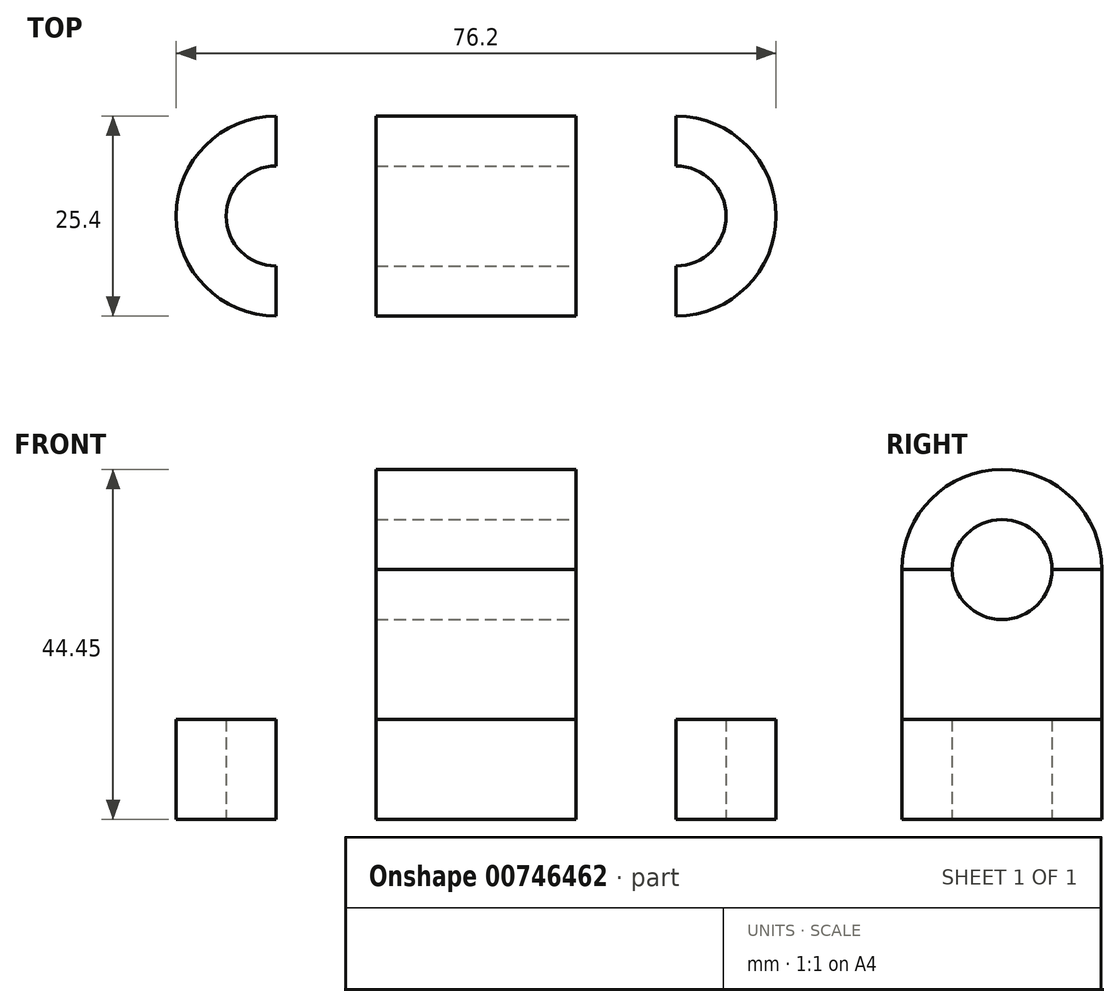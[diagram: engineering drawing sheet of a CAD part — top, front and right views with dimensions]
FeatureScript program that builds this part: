
annotation { "Feature Type Name" : "Feature", "Feature Type Description" : "" }
export const myFeature = defineFeature(function(context is Context, id is Id, definition is map)
    precondition{}
    {
        {
            var Q0;
            Q0=qCreatedBy(makeId("Top.planeOp"),FACE);
            var sketch = newSketch(context, id + "F0", { "sketchPlane" : qUnion([Q0])});
            skLineSegment(sketch, "E0.bottom", {"start": v(0, 0) * mm, "end": v(50.8, 0) * mm});
            skLineSegment(sketch, "E0.top", {"start": v(0, 25.4) * mm, "end": v(50.8, 25.4) * mm});
            skLineSegment(sketch, "E0.left", {"start": v(0, 0) * mm, "end": v(0, 25.4) * mm});
            skLineSegment(sketch, "E0.right", {"start": v(50.8, 0) * mm, "end": v(50.8, 25.4) * mm});
            skArc(sketch, "E1", {"start": v(50.8, 0) * mm, "mid": v(63.5, 12.7) * mm, "end": v(50.8, 25.4) * mm});
            skArc(sketch, "E2", {"start": v(0, 25.4) * mm, "mid": v(-12.7, 12.7) * mm, "end": v(0, 0) * mm});
            skCircle(sketch, "E3", {"center": v(50.8, 12.7) * mm, "radius": 6.35 * mm});
            skCircle(sketch, "E4", {"center": v(0, 12.7) * mm, "radius": 6.35 * mm});
            skLineSegment(sketch, "E5", {"start": v(38.1, 25.4) * mm, "end": v(38.1, 0) * mm});
            skLineSegment(sketch, "E6", {"start": v(38.1, 0) * mm, "end": v(12.7, 0) * mm});
            skLineSegment(sketch, "E7", {"start": v(12.7, 0) * mm, "end": v(12.7, 25.4) * mm});
            skLineSegment(sketch, "E8", {"start": v(12.7, 25.4) * mm, "end": v(38.1, 25.4) * mm});
            skSolve(sketch);
        }
        {
            var Q0;
            {var subQ0=sQuery(id+"F0.wireOp",EDGE,"E2");Q0=makeQuery(id+"F0.imprint","IMPRINT",FACE,{"disambiguationData":[TD([[makeQuery(id+"F0.imprint","IMPRINT",EDGE,{"derivedFrom":subQ0}),1.0]])]});}
            var Q1;
            {var subQ5=sQuery(id+"F0.wireOp",EDGE,"E0.bottom");Q1=makeQuery(id+"F0.imprint","IMPRINT",FACE,{"disambiguationData":[TD([[makeQuery(id+"F0.imprint","IMPRINT",EDGE,{"derivedFrom":subQ5}),1.0]])]});}
            var Q2;
            {var subQ0=sQuery(id+"F0.wireOp",EDGE,"E1");Q2=makeQuery(id+"F0.imprint","IMPRINT",FACE,{"disambiguationData":[TD([[makeQuery(id+"F0.imprint","IMPRINT",EDGE,{"derivedFrom":subQ0}),1.0]])]});}
            extrude(context, id + "F1", {"entities" : qUnion([Q0, Q1, Q2]), "depth" : 12.7 * mm, "offsetDistance" : 25.4 * mm});
        }
        {
            var Q0;
            Q0=makeQuery(id+"F0.imprint","IMPRINT",FACE,{"disambiguationData":[TD([[makeQuery(id+"F0.imprint","IMPRINT",EDGE,{"derivedFrom":sQuery(id+"F0.wireOp",EDGE,"E5")}),-1.0]])]});
            extrude(context, id + "F2", {"entities" : qUnion([Q0]), "depth" : 31.75 * mm, "offsetDistance" : 25.4 * mm});
        }
        {
            var Q0;
            Q0=makeQuery(id+"F2.opExtrude","SWEPT_FACE",FACE,{"disambiguationData":[OSD([sQuery(id+"F0.wireOp",EDGE,"E5")])]});
            var sketch = newSketch(context, id + "F3", { "sketchPlane" : qUnion([Q0])});
            skArc(sketch, "E9", {"start": v(25.4, 31.75) * mm, "mid": v(12.7, 44.45) * mm, "end": v(0, 31.75) * mm});
            skCircle(sketch, "E10", {"center": v(12.7, 31.75) * mm, "radius": 6.35 * mm});
            skSolve(sketch);
        }
        {
            var Q0;
            {var subQ0=sQuery(id+"F3.wireOp",EDGE,"E9");Q0=makeQuery(id+"F3.imprint","IMPRINT",FACE,{"disambiguationData":[TD([[makeQuery(id+"F3.imprint","IMPRINT",EDGE,{"derivedFrom":subQ0}),1.0]])]});}
            extrude(context, id + "F4", {"entities" : qUnion([Q0]), "oppositeDirection" : true, "depth" : 25.4 * mm, "offsetDistance" : 25.4 * mm});
        }
        {
            var Q0;
            Q0 = qSketchRegion(id + "F3", true);
            extrude(context, id + "F5", {"entities" : qUnion([Q0]), "operationType" : NewBodyOperationType.REMOVE, "oppositeDirection" : true, "depth" : 25.4 * mm, "offsetDistance" : 25.4 * mm});
        }
    });
